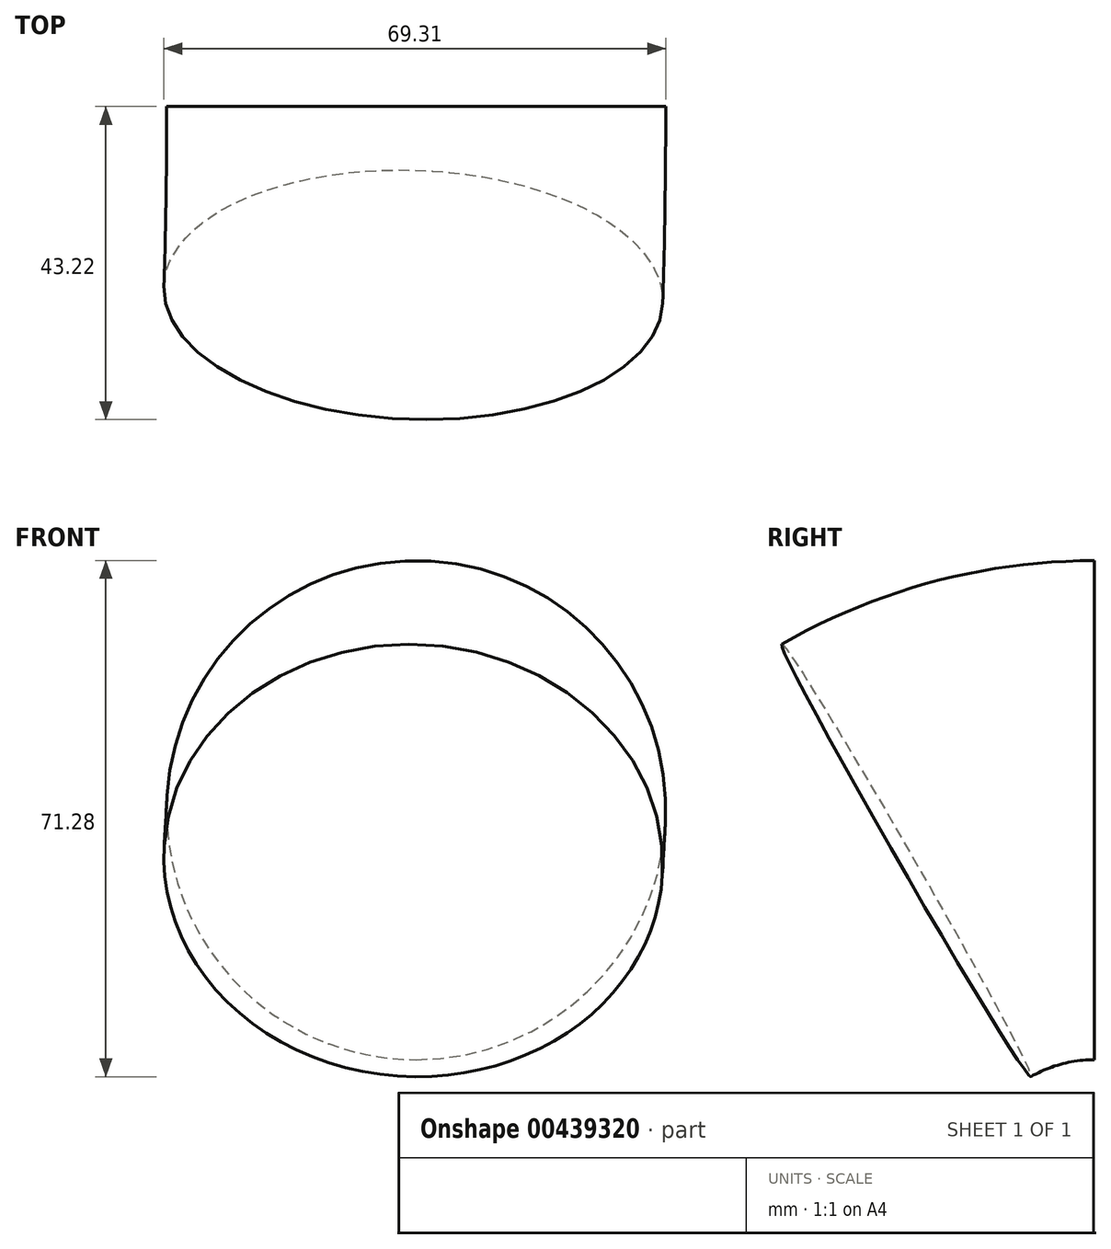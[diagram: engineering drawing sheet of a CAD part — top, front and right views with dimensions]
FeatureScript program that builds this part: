
annotation { "Feature Type Name" : "Feature", "Feature Type Description" : "" }
export const myFeature = defineFeature(function(context is Context, id is Id, definition is map)
    precondition{}
    {
        {
            var Q0;
            Q0=qCreatedBy(makeId("Front.planeOp"),FACE);
            var sketch = newSketch(context, id + "F0", { "sketchPlane" : qUnion([Q0])});
            skCircle(sketch, "E0", {"center": v(0, 0) * mm, "radius": 33.86 * mm});
            skLineSegment(sketch, "E1.bottom", {"start": v(17.2, -11.53) * mm, "end": v(-17.2, -11.53) * mm});
            skLineSegment(sketch, "E1.top", {"start": v(17.2, 11.53) * mm, "end": v(-17.2, 11.53) * mm});
            skLineSegment(sketch, "E1.left", {"start": v(17.2, -11.53) * mm, "end": v(17.2, 11.53) * mm});
            skLineSegment(sketch, "E1.right", {"start": v(-17.2, -11.53) * mm, "end": v(-17.2, 11.53) * mm});
            skSolve(sketch);
        }
        {
            var Q0;
            Q0=makeQuery(id+"F0.imprint","IMPRINT",FACE,{"disambiguationData":[TD([[makeQuery(id+"F0.imprint","IMPRINT",EDGE,{"derivedFrom":sQuery(id+"F0.wireOp",EDGE,"E0")}),1.0]])]});
            extrude(context, id + "F1", {"entities" : qUnion([Q0]), "depth" : 125 * mm});
        }
        {
            var Q0;
            Q0=makeQuery(id+"F1.opExtrude","CAP_EDGE",EDGE,{"disambiguationData":[OSD([sQuery(id+"F0.wireOp",EDGE,"E0")])],"isStart":false});
            chamfer(context, id + "F2", {"entities" : qUnion([Q0]), "width" : 5 * mm, "tangentPropagation" : true});
        }
        {
            var Q0;
            Q0=makeQuery(id+"F1.opExtrude","CAP_EDGE",EDGE,{"disambiguationData":[OSD([sQuery(id+"F0.wireOp",EDGE,"E1.top")])],"isStart":false});
            var Q1;
            Q1=makeQuery(id+"F1.opExtrude","CAP_EDGE",EDGE,{"disambiguationData":[OSD([sQuery(id+"F0.wireOp",EDGE,"E1.right")])],"isStart":false});
            var Q2;
            Q2=makeQuery(id+"F1.opExtrude","CAP_EDGE",EDGE,{"disambiguationData":[OSD([sQuery(id+"F0.wireOp",EDGE,"E1.bottom")])],"isStart":false});
            var Q3;
            Q3=makeQuery(id+"F1.opExtrude","CAP_EDGE",EDGE,{"disambiguationData":[OSD([sQuery(id+"F0.wireOp",EDGE,"E1.left")])],"isStart":false});
            fillet(context, id + "F3", {"entities" : qUnion([Q0, Q1, Q2, Q3]), "radius" : 5 * mm, "tangentPropagation" : true, "allowEdgeOverflow" : false});
        }
        {
            var Q0;
            Q0=qCreatedBy(makeId("Front.planeOp"),FACE);
            var sketch = newSketch(context, id + "F4", { "sketchPlane" : qUnion([Q0])});
            skCircle(sketch, "E2", {"center": v(-44.03, 58.49) * mm, "radius": 34.46 * mm});
            skLineSegment(sketch, "E3", {"start": v(-102.6, 9.83) * mm, "end": v(66.03, 0) * mm});
            skSolve(sketch);
        }
        {
            var Q0;
            Q0=makeQuery(id+"F4.imprint","IMPRINT",FACE,{"disambiguationData":[TD([[makeQuery(id+"F4.imprint","IMPRINT",EDGE,{"derivedFrom":sQuery(id+"F4.wireOp",EDGE,"E2")}),1.0]])]});
            var Q1;
            Q1=sQuery(id+"F4.wireOp",EDGE,"E3");
            revolve(context, id + "F5", {"entities" : qUnion([Q0]), "axis" : qUnion([Q1]), "revolveType" : RevolveType.ONE_DIRECTION, "angle" : 30 * degree});
        }
        {
            var Q0;
            Q0=makeQuery(id+"F1.opExtrude","SWEPT_BODY",BODY,{"disambiguationData":[OSD([sQuery(id+"F0.wireOp",EDGE,"E0"),sQuery(id+"F0.wireOp",EDGE,"E1.bottom"),sQuery(id+"F0.wireOp",EDGE,"E1.top"),sQuery(id+"F0.wireOp",EDGE,"E1.left"),sQuery(id+"F0.wireOp",EDGE,"E1.right")])]});
            deleteBodies(context, id + "F6", {"entities" : qUnion([Q0])});
        }
    });
